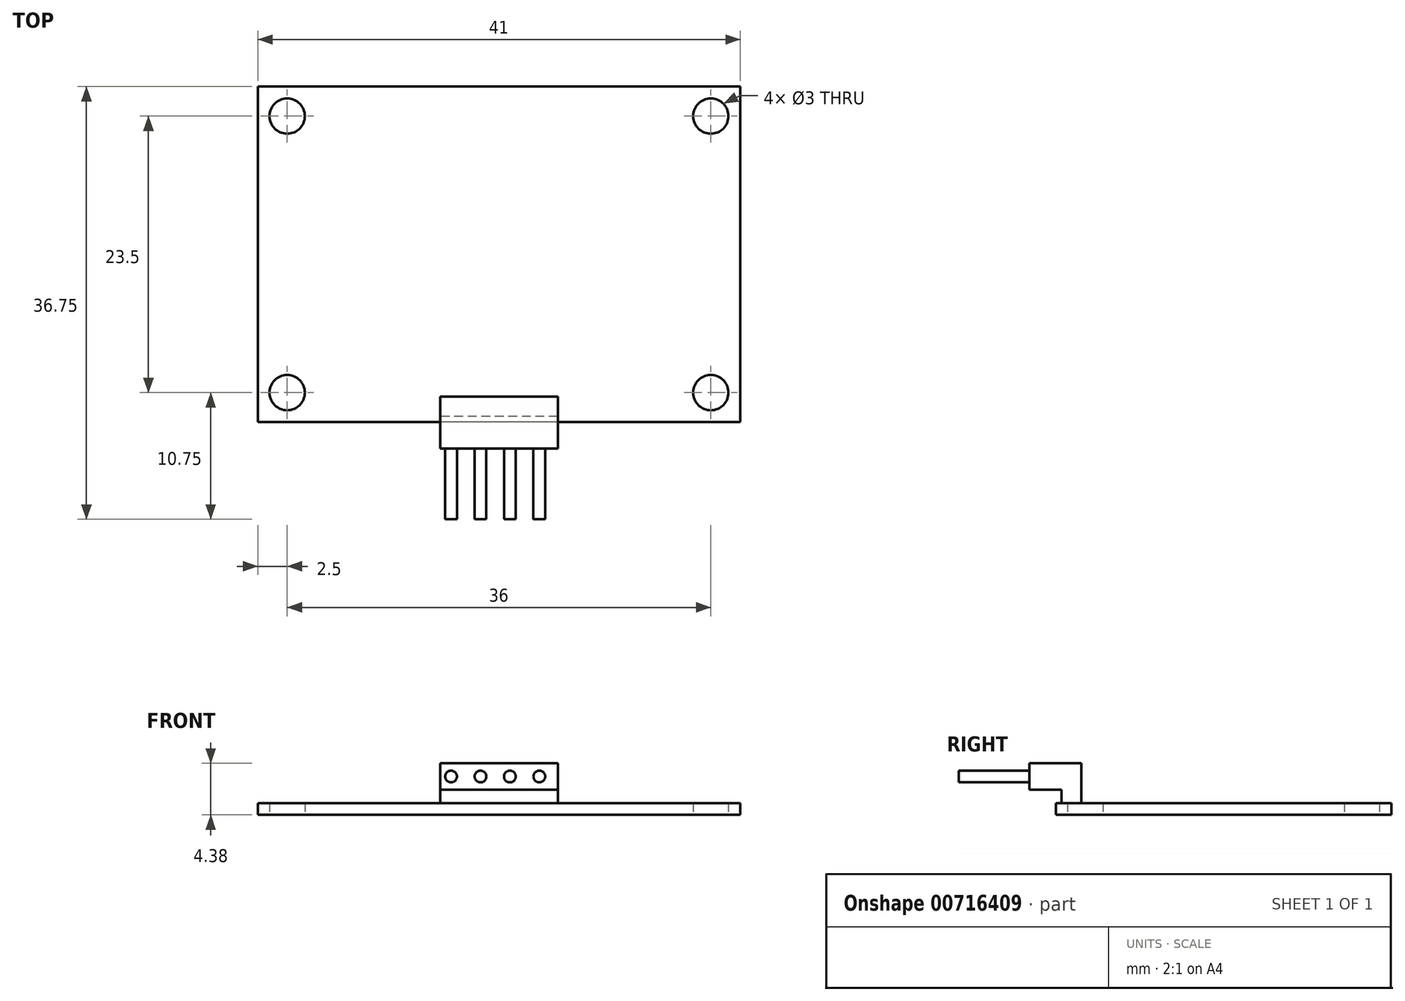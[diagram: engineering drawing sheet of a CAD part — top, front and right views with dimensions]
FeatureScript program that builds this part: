
annotation { "Feature Type Name" : "Feature", "Feature Type Description" : "" }
export const myFeature = defineFeature(function(context is Context, id is Id, definition is map)
    precondition{}
    {
        {
            var Q0;
            Q0=qCreatedBy(makeId("Top.planeOp"),FACE);
            var sketch = newSketch(context, id + "F0", { "sketchPlane" : qUnion([Q0])});
            skLineSegment(sketch, "E0.bottom", {"start": v(20.5, -14.25) * mm, "end": v(-20.5, -14.25) * mm});
            skLineSegment(sketch, "E0.top", {"start": v(20.5, 14.25) * mm, "end": v(-20.5, 14.25) * mm});
            skLineSegment(sketch, "E0.left", {"start": v(20.5, -14.25) * mm, "end": v(20.5, 14.25) * mm});
            skLineSegment(sketch, "E0.right", {"start": v(-20.5, -14.25) * mm, "end": v(-20.5, 14.25) * mm});
            skPoint(sketch, "E0.middle", {"position": v(0, 0) * mm});
            skCircle(sketch, "E1", {"center": v(18, -11.75) * mm, "radius": 1.5 * mm});
            skCircle(sketch, "E2.MirrorC", {"center": v(-18, -11.75) * mm, "radius": 1.5 * mm});
            skCircle(sketch, "E3.MirrorC", {"center": v(-18, 11.75) * mm, "radius": 1.5 * mm});
            skCircle(sketch, "E4.MirrorC", {"center": v(18, 11.75) * mm, "radius": 1.5 * mm});
            skSolve(sketch);
        }
        {
            var Q0;
            Q0 = qSketchRegion(id + "F0", true);
            extrude(context, id + "F1", {"entities" : qUnion([Q0]), "depth" : 1 * mm, "offsetDistance" : 25 * mm});
        }
        {
            var Q0;
            Q0=qCreatedBy(makeId("Right.planeOp"),FACE);
            var sketch = newSketch(context, id + "F2", { "sketchPlane" : qUnion([Q0])});
            skLineSegment(sketch, "E5", {"start": v(-12.1, 0.99) * mm, "end": v(-12.1, 4.38) * mm});
            skLineSegment(sketch, "E6", {"start": v(-12.1, 4.38) * mm, "end": v(-16.5, 4.38) * mm});
            skLineSegment(sketch, "E7", {"start": v(-16.5, 4.38) * mm, "end": v(-16.5, 2.15) * mm});
            skLineSegment(sketch, "E8", {"start": v(-16.5, 2.15) * mm, "end": v(-13.77, 2.15) * mm});
            skLineSegment(sketch, "E9", {"start": v(-13.77, 2.15) * mm, "end": v(-13.77, 0.99) * mm});
            skLineSegment(sketch, "E10", {"start": v(-13.77, 0.99) * mm, "end": v(-12.1, 0.99) * mm});
            skSolve(sketch);
        }
        {
            var Q0;
            Q0 = qSketchRegion(id + "F2", true);
            extrude(context, id + "F3", {"entities" : qUnion([Q0]), "operationType" : NewBodyOperationType.ADD, "depth" : 5 * mm, "offsetDistance" : 25 * mm, "hasSecondDirection" : true, "secondDirectionOppositeDirection" : true, "secondDirectionDepth" : 5 * mm});
        }
        {
            var Q0;
            Q0=makeQuery(id+"F3.opExtrude","SWEPT_FACE",FACE,{"disambiguationData":[OSD([sQuery(id+"F2.wireOp",EDGE,"E7")])]});
            var sketch = newSketch(context, id + "F4", { "sketchPlane" : qUnion([Q0])});
            skCircle(sketch, "E11", {"center": v(-4.07, 3.26) * mm, "radius": 0.5 * mm});
            skPoint(sketch, "E11.centerSnap0", {"position": v(5, 3.26) * mm});
            skCircle(sketch, "E12.1.0.0", {"center": v(-1.57, 3.26) * mm, "radius": 0.5 * mm});
            skCircle(sketch, "E12.2.0.0", {"center": v(0.93, 3.26) * mm, "radius": 0.5 * mm});
            skCircle(sketch, "E12.3.0.0", {"center": v(3.43, 3.26) * mm, "radius": 0.5 * mm});
            skLineSegment(sketch, "E12.direction1", {"start": v(-4.07, 3.26) * mm, "end": v(-1.57, 3.26) * mm, "construction": true});
            skSolve(sketch);
        }
        {
            var Q0;
            Q0 = qSketchRegion(id + "F4", true);
            extrude(context, id + "F5", {"entities" : qUnion([Q0]), "operationType" : NewBodyOperationType.ADD, "depth" : 6 * mm, "offsetDistance" : 25 * mm});
        }
    });
